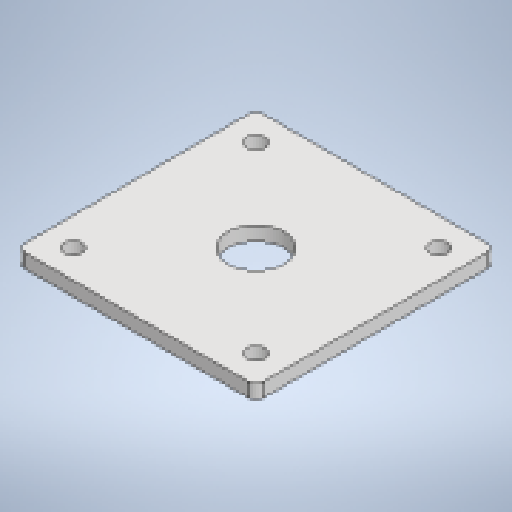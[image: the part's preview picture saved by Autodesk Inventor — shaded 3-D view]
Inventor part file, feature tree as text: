
AUTODESK INVENTOR PART (.ipt)
format: ipt  version: 2025.1 (Build 291241020, 241B)  size: 204,800 bytes
history: native  units: mm
features: extrude x2, sketch x2, pattern_circular x1, fillet x1, other x1
ambient origin geometry x8: Origin, YZ Plane, XZ Plane, XY Plane, X Axis, Y Axis, Z Axis, Center Point
bodies: Solid1 (feature_tree)
feature tree (7):
  extrude  "Extrusion1"  Depth=10.0mm TaperAngle=0.0deg
  extrude  "Extrusion2"  Depth=170.0mm
  pattern_circular  "Circular Pattern2"  [2 undecoded]
  fillet  "Fillet1"  Radius=40.0mm
  sketch  "Sketch1"  dims[d0=40.0mm d2=10.0mm d3=0.0mm]
  sketch  "Sketch4"  dims[d6=10.0mm d13=170.0mm d16=0.0mm d17=0.0mm d18=40.0mm d19=360.0deg d21=5.0mm d22=183.847763mm d23=13.0mm d24=65.0mm d25=65.0mm]
  other  "Definition1"
note: 2 required parameter values undecoded (feature->parameter linkage not recoverable at this tier; creation-order binding heuristic only, values carry confidence <= 0.55)
